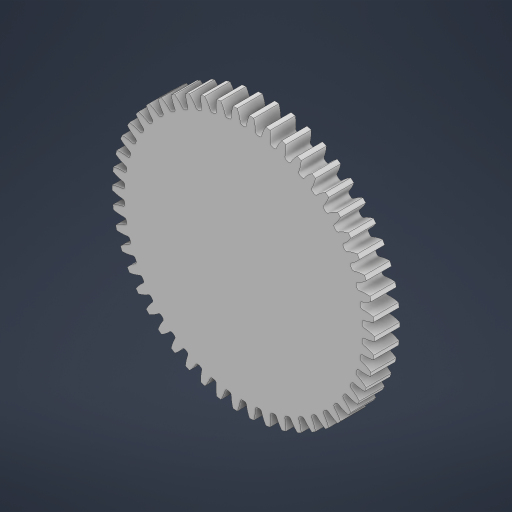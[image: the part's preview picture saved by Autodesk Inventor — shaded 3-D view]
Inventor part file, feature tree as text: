
AUTODESK INVENTOR PART (.ipt)
format: ipt  version: 2024.1 (Build 281209000, 209)  size: 437,248 bytes
history: native  units: in
note: dims shown in document units (in); Inventor stores cm internally (conversion verified against a paired STEP export)
features: extrude x2, pattern_circular x1
ambient origin geometry x8: Origin, YZ Plane, XZ Plane, XY Plane, X Axis, Y Axis, Z Axis, Center Point
bodies: Solid1 (feature_tree)
feature tree (3):
  extrude  "Extrusion1"  Depth=0.15in
  extrude  "Extrusion2"  TaperAngle=0.0deg  [1 undecoded]
  pattern_circular  "Circular Pattern1"  [2 undecoded]
note: 3 required parameter values undecoded (feature->parameter linkage not recoverable at this tier; creation-order binding heuristic only, values carry confidence <= 0.55)
